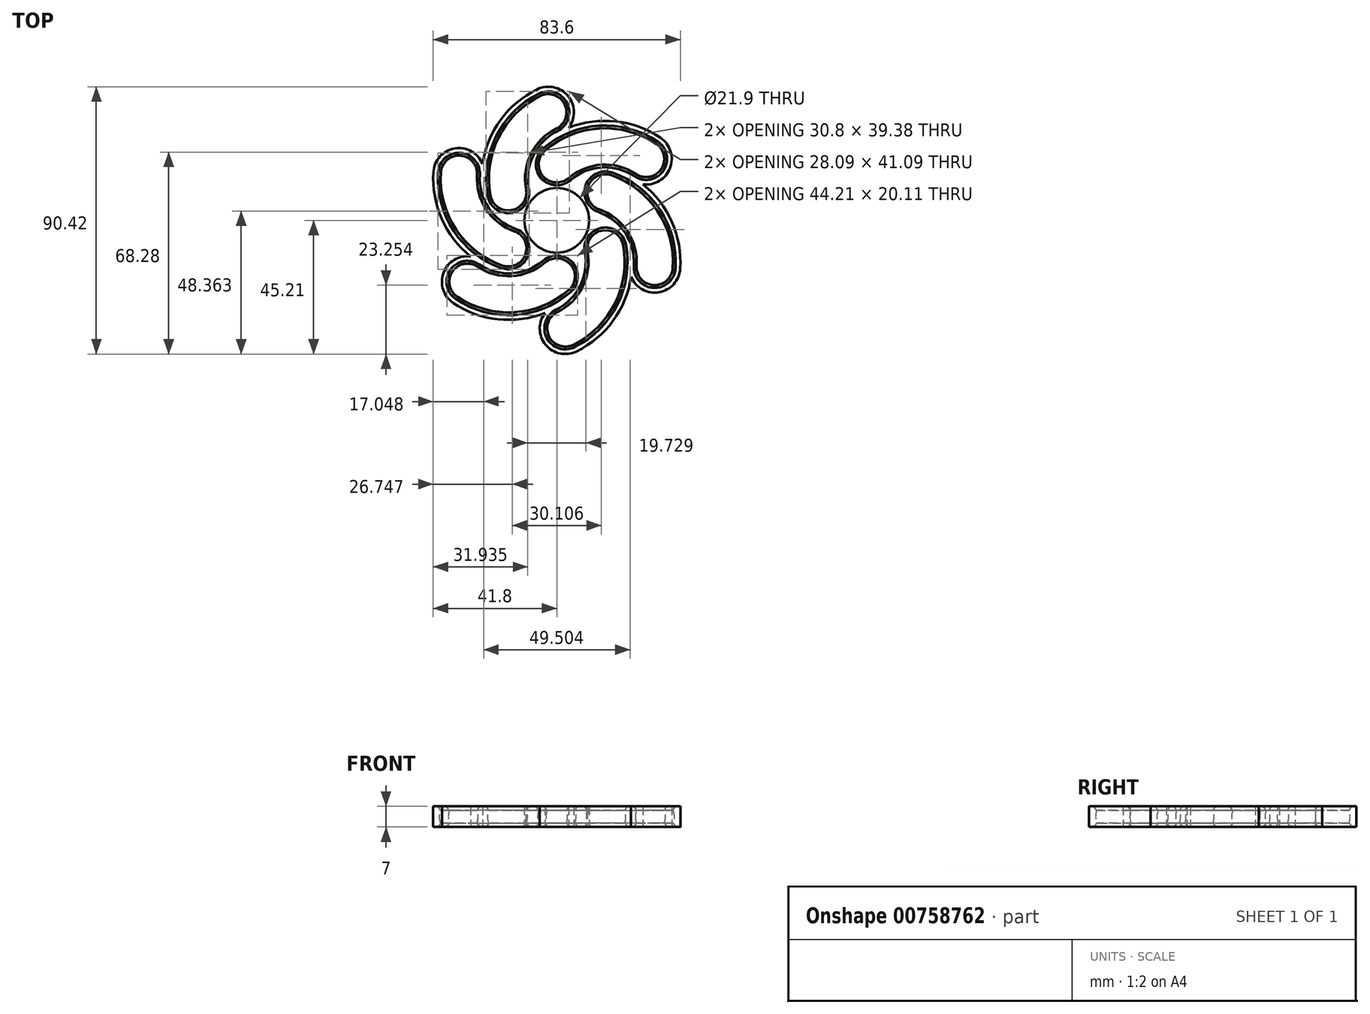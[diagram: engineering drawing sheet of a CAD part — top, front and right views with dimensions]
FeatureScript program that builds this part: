
annotation { "Feature Type Name" : "Feature", "Feature Type Description" : "" }
export const myFeature = defineFeature(function(context is Context, id is Id, definition is map)
    precondition{}
    {
        {
            var Q0;
            Q0=qCreatedBy(makeId("Top.planeOp"),FACE);
            var sketch = newSketch(context, id + "F0", { "sketchPlane" : qUnion([Q0])});
            skArc(sketch, "E0", {"start": v(6.97, 8.45) * mm, "mid": v(-0.32, 10.95) * mm, "end": v(-7.45, 8.02) * mm});
            skPoint(sketch, "E1", {"position": v(0, -24.5) * mm});
            skLineSegment(sketch, "E2", {"start": v(0, 0) * mm, "end": v(0, 18.95) * mm, "construction": true});
            skArc(sketch, "E3", {"start": v(25.4, 13.58) * mm, "mid": v(12.95, 16) * mm, "end": v(2.52, 8.78) * mm});
            skArc(sketch, "E4.0", {"start": v(30.22, 20.77) * mm, "mid": v(14.8, 24.95) * mm, "end": v(0, 18.95) * mm});
            skArc(sketch, "E5.0", {"start": v(35.03, 27.96) * mm, "mid": v(14.7, 33.61) * mm, "end": v(-5, 26.04) * mm});
            skArc(sketch, "E6", {"start": v(25.4, 13.58) * mm, "mid": v(37.4, 15.96) * mm, "end": v(35.03, 27.96) * mm});
            skArc(sketch, "E7.0", {"start": v(12.06, 14.62) * mm, "mid": v(0, 18.95) * mm, "end": v(-12.06, 14.62) * mm, "construction": true});
            skLineSegment(sketch, "E8", {"start": v(-7.45, 8.02) * mm, "end": v(-9.2, 16.57) * mm});
            skLineSegment(sketch, "E9", {"start": v(-9.2, 16.57) * mm, "end": v(-5, 26.04) * mm});
            skSolve(sketch);
        }
        {
            var Q0;
            {var subQ4=sQuery(id+"F0.wireOp",EDGE,"PiiM7Q08-lsxY-islm-UEzh-ksM0SnnuY6FK");Q0=makeQuery(id+"F0.imprint","IMPRINT",FACE,{"disambiguationData":[TD([[makeQuery(id+"F0.imprint","IMPRINT",EDGE,{"derivedFrom":subQ4}),-1.0]])]});}
            var Q1;
            Q1=makeQuery(id+"F0.imprint","IMPRINT",FACE,{"disambiguationData":[TD([[makeQuery(id+"F0.imprint","IMPRINT",EDGE,{"derivedFrom":sQuery(id+"F0.wireOp",EDGE,"E0")}),-1.0]])]});
            var Q2;
            {var subQ4=sQuery(id+"F0.wireOp",EDGE,"QqK0a54Q-URX9-TbrE-nkqz-KXdzGL0UVco7");Q2=makeQuery(id+"F0.imprint","IMPRINT",FACE,{"disambiguationData":[TD([[makeQuery(id+"F0.imprint","IMPRINT",EDGE,{"derivedFrom":subQ4}),-1.0]])]});}
            var Q3;
            {var subQ5=sQuery(id+"F0.wireOp",EDGE,"PiiM7Q08-lsxY-islm-UEzh-ksM0SnnuY6FK");Q3=makeQuery(id+"F0.imprint","IMPRINT",FACE,{"disambiguationData":[TD([[makeQuery(id+"F0.imprint","IMPRINT",EDGE,{"derivedFrom":subQ5}),1.0]])]});}
            var Q4;
            {var subQ1=sQuery(id+"F0.wireOp",EDGE,"E5.0");Q4=makeQuery(id+"F0.imprint","IMPRINT",FACE,{"disambiguationData":[TD([[makeQuery(id+"F0.imprint","IMPRINT",EDGE,{"derivedFrom":subQ1}),1.0]])]});}
            extrude(context, id + "F1", {"entities" : qUnion([Q0, Q1, Q2, Q3, Q4]), "endBound" : BoundingType.SYMMETRIC, "depth" : 7 * mm, "offsetDistance" : 25 * mm});
        }
        {
            var Q0;
            Q0=makeQuery(id+"F1.opExtrude","SWEPT_EDGE",EDGE,{"disambiguationData":[OSD([sQuery(id+"F0.wireOp",EDGE,"E3"),sQuery(id+"F0.wireOp",EDGE,"E6")])]});
            var Q1;
            Q1=sQuery(id+"F0.wireOp",VERTEX,"E5.0.start");
            cPlane(context, id + "F2", {"entities" : qUnion([Q0, Q1]), "cplaneType" : CPlaneType.LINE_ANGLE, "offset" : 25 * mm, "angle" : 0 * degree, "width" : 150 * mm, "height" : 150 * mm});
        }
        {
            var Q0;
            Q0=qCreatedBy(id+"F2.planeOp",FACE);
            var sketch = newSketch(context, id + "F3", { "sketchPlane" : qUnion([Q0])});
            skLineSegment(sketch, "E10", {"start": v(34.08, 6.5) * mm, "end": v(34.08, -6.5) * mm});
            skArc(sketch, "E11", {"start": v(34.08, -6.5) * mm, "mid": v(40.58, 0) * mm, "end": v(34.08, 6.5) * mm});
            skArc(sketch, "E12.MirrorCS", {"start": v(34.08, -6.5) * mm, "mid": v(27.58, 0) * mm, "end": v(34.08, 6.5) * mm});
            skSolve(sketch);
        }
        {
            var Q0;
            Q0=makeQuery(id+"F3.imprint","IMPRINT",FACE,{"disambiguationData":[TD([[makeQuery(id+"F3.imprint","IMPRINT",EDGE,{"derivedFrom":sQuery(id+"F3.wireOp",EDGE,"E10")}),1.0]])]});
            var Q1;
            Q1=makeQuery(id+"F3.imprint","IMPRINT",FACE,{"disambiguationData":[TD([[makeQuery(id+"F3.imprint","IMPRINT",EDGE,{"derivedFrom":sQuery(id+"F3.wireOp",EDGE,"E10")}),-1.0]])]});
            var Q2;
            Q2=sQuery(id+"F0.wireOp",EDGE,"E4.0");
            sweep(context, id + "F4", {"operationType" : NewBodyOperationType.REMOVE, "profiles" : qUnion([Q0, Q1]), "path" : qUnion([Q2])});
        }
        {
            var Q0;
            Q0=makeQuery(id+"F3.imprint","IMPRINT",FACE,{"disambiguationData":[TD([[makeQuery(id+"F3.imprint","IMPRINT",EDGE,{"derivedFrom":sQuery(id+"F3.wireOp",EDGE,"E10")}),1.0]])]});
            var Q1;
            Q1=sQuery(id+"F3.wireOp",EDGE,"E10");
            revolve(context, id + "F5", {"operationType" : NewBodyOperationType.REMOVE, "surfaceOperationType" : NewSurfaceOperationType.NEW, "entities" : qUnion([Q0]), "axis" : qUnion([Q1]), "revolveType" : RevolveType.ONE_DIRECTION, "angle" : 180 * degree});
        }
        {
            var Q0;
            Q0=makeQuery(id+"F4.boolean.opBoolean","COPY",FACE,{"derivedFrom":makeQuery(id+"F4.opSweep","CAP_FACE",FACE,{"disambiguationData":[OSD([sQuery(id+"F0.wireOp",VERTEX,"E4.0.end"),sQuery(id+"F3.wireOp",EDGE,"E11"),sQuery(id+"F3.wireOp",EDGE,"E12.MirrorCS")])],"isStart":false})});
            var sketch = newSketch(context, id + "F6", { "sketchPlane" : qUnion([Q0])});
            skLineSegment(sketch, "E13", {"start": v(20.86, 0) * mm, "end": v(7.86, 0) * mm});
            skArc(sketch, "E14", {"start": v(7.86, 0) * mm, "mid": v(14.36, -6.5) * mm, "end": v(20.86, 0) * mm});
            skSolve(sketch);
        }
        {
            var Q0;
            {var subQ1=makeQuery(id+"F4.boolean.opBoolean","INTERSECT",EDGE,{"derivedFrom":[makeQuery(id+"F1.opExtrude","CAP_FACE",FACE,{"disambiguationData":[OSD([sQuery(id+"F0.wireOp",EDGE,"E0"),sQuery(id+"F0.wireOp",EDGE,"Lb8NWhK4-ym9p-KzVv-z8Fr-7k6zUVGv0M9w"),sQuery(id+"F0.wireOp",EDGE,"QqK0a54Q-URX9-TbrE-nkqz-KXdzGL0UVco7"),sQuery(id+"F0.wireOp",EDGE,"E3"),sQuery(id+"F0.wireOp",EDGE,"E5.0"),sQuery(id+"F0.wireOp",EDGE,"E6"),sQuery(id+"F0.wireOp",EDGE,"nqTzWoM8-xc7r-Lhgo-26Yi-vVSrXjbg86Ji")])],"isStart":true}),makeQuery(id+"F4.opSweep","CAP_FACE",FACE,{"disambiguationData":[OSD([sQuery(id+"F0.wireOp",VERTEX,"I2wmlmdm-DSrS-oub0-GOcV-EtuJTHkaWZzk.end"),sQuery(id+"F3.wireOp",EDGE,"E11"),sQuery(id+"F3.wireOp",EDGE,"E12.MirrorCS")])],"isStart":false})]});Q0=makeQuery(id+"F6.imprint","IMPRINT",FACE,{"disambiguationData":[TD([[makeQuery(id+"F6.imprint","IMPRINT",EDGE,{"derivedFrom":subQ1}),-1.0]])]});}
            var Q1;
            {var subQ0=sQuery(id+"F6.wireOp",EDGE,"E13");Q1=makeQuery(id+"F6.imprint","IMPRINT",FACE,{"disambiguationData":[TD([[makeQuery(id+"F6.imprint","IMPRINT",EDGE,{"derivedFrom":subQ0}),1.0]])]});}
            var Q2;
            Q2=sQuery(id+"F6.wireOp",EDGE,"E13");
            revolve(context, id + "F7", {"operationType" : NewBodyOperationType.REMOVE, "surfaceOperationType" : NewSurfaceOperationType.NEW, "entities" : qUnion([Q0, Q1]), "axis" : qUnion([Q2]), "revolveType" : RevolveType.FULL, "oppositeDirection" : true});
        }
        {
            var Q0;
            Q0=qCreatedBy(makeId("Front.planeOp"),FACE);
            var sketch = newSketch(context, id + "F8", { "sketchPlane" : qUnion([Q0])});
            skLineSegment(sketch, "E15", {"start": v(0, -9.37) * mm, "end": v(0, 10.86) * mm, "construction": true});
            skSolve(sketch);
        }
        {
            var Q0;
            Q0=makeQuery(id+"F1.opExtrude","SWEPT_BODY",BODY,{"disambiguationData":[OSD([sQuery(id+"F0.wireOp",EDGE,"E0"),sQuery(id+"F0.wireOp",EDGE,"Lb8NWhK4-ym9p-KzVv-z8Fr-7k6zUVGv0M9w"),sQuery(id+"F0.wireOp",EDGE,"QqK0a54Q-URX9-TbrE-nkqz-KXdzGL0UVco7"),sQuery(id+"F0.wireOp",EDGE,"E3"),sQuery(id+"F0.wireOp",EDGE,"E5.0"),sQuery(id+"F0.wireOp",EDGE,"E6"),sQuery(id+"F0.wireOp",EDGE,"nqTzWoM8-xc7r-Lhgo-26Yi-vVSrXjbg86Ji")])]});
            var Q1;
            Q1=sQuery(id+"F8.wireOp",EDGE,"E15");
            circularPattern(context, id + "F9", {"operationType" : NewBodyOperationType.ADD, "entities" : qUnion([Q0]), "axis" : qUnion([Q1]), "angle" : 360 * degree, "instanceCount" : 6, "equalSpace" : true});
        }
        {
            var Q0;
            Q0=makeQuery(id+"F9.opPattern","COPY",EDGE,{"derivedFrom":makeQuery(id+"F4.boolean.opBoolean","INTERSECT",EDGE,{"disambiguationData":[OD(1.0)],"derivedFrom":[makeQuery(id+"F1.opExtrude","CAP_FACE",FACE,{"disambiguationData":[OSD([sQuery(id+"F0.wireOp",EDGE,"E0"),sQuery(id+"F0.wireOp",EDGE,"E3"),sQuery(id+"F0.wireOp",EDGE,"E5.0"),sQuery(id+"F0.wireOp",EDGE,"E6"),sQuery(id+"F0.wireOp",EDGE,"nqTzWoM8-xc7r-Lhgo-26Yi-vVSrXjbg86Ji")])],"isStart":false}),makeQuery(id+"F4.opSweep","SWEPT_FACE",FACE,{"disambiguationData":[OSD([sQuery(id+"F0.wireOp",EDGE,"E4.0"),sQuery(id+"F3.wireOp",EDGE,"E11"),sQuery(id+"F3.wireOp",EDGE,"E12.MirrorCS")])]})]}),"instanceName":"3"});
            var Q1;
            Q1=makeQuery(id+"F9.opPattern","COPY",EDGE,{"derivedFrom":makeQuery(id+"F4.boolean.opBoolean","INTERSECT",EDGE,{"disambiguationData":[OD(0.0)],"derivedFrom":[makeQuery(id+"F1.opExtrude","CAP_FACE",FACE,{"disambiguationData":[OSD([sQuery(id+"F0.wireOp",EDGE,"E0"),sQuery(id+"F0.wireOp",EDGE,"E3"),sQuery(id+"F0.wireOp",EDGE,"E5.0"),sQuery(id+"F0.wireOp",EDGE,"E6"),sQuery(id+"F0.wireOp",EDGE,"nqTzWoM8-xc7r-Lhgo-26Yi-vVSrXjbg86Ji")])],"isStart":false}),makeQuery(id+"F4.opSweep","SWEPT_FACE",FACE,{"disambiguationData":[OSD([sQuery(id+"F0.wireOp",EDGE,"E4.0"),sQuery(id+"F3.wireOp",EDGE,"E11"),sQuery(id+"F3.wireOp",EDGE,"E12.MirrorCS")])]})]}),"instanceName":"4"});
            var Q2;
            Q2=makeQuery(id+"F9.opPattern","COPY",EDGE,{"derivedFrom":makeQuery(id+"F4.boolean.opBoolean","INTERSECT",EDGE,{"disambiguationData":[OD(1.0)],"derivedFrom":[makeQuery(id+"F1.opExtrude","CAP_FACE",FACE,{"disambiguationData":[OSD([sQuery(id+"F0.wireOp",EDGE,"E0"),sQuery(id+"F0.wireOp",EDGE,"E3"),sQuery(id+"F0.wireOp",EDGE,"E5.0"),sQuery(id+"F0.wireOp",EDGE,"E6"),sQuery(id+"F0.wireOp",EDGE,"nqTzWoM8-xc7r-Lhgo-26Yi-vVSrXjbg86Ji")])],"isStart":false}),makeQuery(id+"F4.opSweep","SWEPT_FACE",FACE,{"disambiguationData":[OSD([sQuery(id+"F0.wireOp",EDGE,"E4.0"),sQuery(id+"F3.wireOp",EDGE,"E11"),sQuery(id+"F3.wireOp",EDGE,"E12.MirrorCS")])]})]}),"instanceName":"5"});
            var Q3;
            Q3=makeQuery(id+"F9.opPattern","COPY",EDGE,{"derivedFrom":makeQuery(id+"F4.boolean.opBoolean","INTERSECT",EDGE,{"disambiguationData":[OD(0.0)],"derivedFrom":[makeQuery(id+"F1.opExtrude","CAP_FACE",FACE,{"disambiguationData":[OSD([sQuery(id+"F0.wireOp",EDGE,"E0"),sQuery(id+"F0.wireOp",EDGE,"E3"),sQuery(id+"F0.wireOp",EDGE,"E5.0"),sQuery(id+"F0.wireOp",EDGE,"E6"),sQuery(id+"F0.wireOp",EDGE,"nqTzWoM8-xc7r-Lhgo-26Yi-vVSrXjbg86Ji")])],"isStart":false}),makeQuery(id+"F4.opSweep","SWEPT_FACE",FACE,{"disambiguationData":[OSD([sQuery(id+"F0.wireOp",EDGE,"E4.0"),sQuery(id+"F3.wireOp",EDGE,"E11"),sQuery(id+"F3.wireOp",EDGE,"E12.MirrorCS")])]})]}),"instanceName":"6"});
            var Q4;
            Q4=makeQuery(id+"F4.boolean.opBoolean","INTERSECT",EDGE,{"disambiguationData":[OD(0.0)],"derivedFrom":[makeQuery(id+"F1.opExtrude","CAP_FACE",FACE,{"disambiguationData":[OSD([sQuery(id+"F0.wireOp",EDGE,"E0"),sQuery(id+"F0.wireOp",EDGE,"E3"),sQuery(id+"F0.wireOp",EDGE,"E5.0"),sQuery(id+"F0.wireOp",EDGE,"E6"),sQuery(id+"F0.wireOp",EDGE,"nqTzWoM8-xc7r-Lhgo-26Yi-vVSrXjbg86Ji")])],"isStart":false}),makeQuery(id+"F4.opSweep","SWEPT_FACE",FACE,{"disambiguationData":[OSD([sQuery(id+"F0.wireOp",EDGE,"E4.0"),sQuery(id+"F3.wireOp",EDGE,"E11"),sQuery(id+"F3.wireOp",EDGE,"E12.MirrorCS")])]})]});
            var Q5;
            Q5=makeQuery(id+"F9.opPattern","COPY",EDGE,{"derivedFrom":makeQuery(id+"F4.boolean.opBoolean","INTERSECT",EDGE,{"disambiguationData":[OD(0.0)],"derivedFrom":[makeQuery(id+"F1.opExtrude","CAP_FACE",FACE,{"disambiguationData":[OSD([sQuery(id+"F0.wireOp",EDGE,"E0"),sQuery(id+"F0.wireOp",EDGE,"E3"),sQuery(id+"F0.wireOp",EDGE,"E5.0"),sQuery(id+"F0.wireOp",EDGE,"E6"),sQuery(id+"F0.wireOp",EDGE,"nqTzWoM8-xc7r-Lhgo-26Yi-vVSrXjbg86Ji")])],"isStart":false}),makeQuery(id+"F4.opSweep","SWEPT_FACE",FACE,{"disambiguationData":[OSD([sQuery(id+"F0.wireOp",EDGE,"E4.0"),sQuery(id+"F3.wireOp",EDGE,"E11"),sQuery(id+"F3.wireOp",EDGE,"E12.MirrorCS")])]})]}),"instanceName":"1"});
            var Q6;
            Q6=makeQuery(id+"F9.opPattern","COPY",EDGE,{"derivedFrom":makeQuery(id+"F4.boolean.opBoolean","INTERSECT",EDGE,{"disambiguationData":[OD(0.0)],"derivedFrom":[makeQuery(id+"F1.opExtrude","CAP_FACE",FACE,{"disambiguationData":[OSD([sQuery(id+"F0.wireOp",EDGE,"E0"),sQuery(id+"F0.wireOp",EDGE,"E3"),sQuery(id+"F0.wireOp",EDGE,"E5.0"),sQuery(id+"F0.wireOp",EDGE,"E6"),sQuery(id+"F0.wireOp",EDGE,"nqTzWoM8-xc7r-Lhgo-26Yi-vVSrXjbg86Ji")])],"isStart":false}),makeQuery(id+"F4.opSweep","SWEPT_FACE",FACE,{"disambiguationData":[OSD([sQuery(id+"F0.wireOp",EDGE,"E4.0"),sQuery(id+"F3.wireOp",EDGE,"E11"),sQuery(id+"F3.wireOp",EDGE,"E12.MirrorCS")])]})]}),"instanceName":"2"});
            var Q7;
            Q7=makeQuery(id+"F9.opPattern","COPY",EDGE,{"derivedFrom":makeQuery(id+"F4.boolean.opBoolean","INTERSECT",EDGE,{"disambiguationData":[OD(1.0)],"derivedFrom":[makeQuery(id+"F1.opExtrude","CAP_FACE",FACE,{"disambiguationData":[OSD([sQuery(id+"F0.wireOp",EDGE,"E0"),sQuery(id+"F0.wireOp",EDGE,"E3"),sQuery(id+"F0.wireOp",EDGE,"E5.0"),sQuery(id+"F0.wireOp",EDGE,"E6"),sQuery(id+"F0.wireOp",EDGE,"nqTzWoM8-xc7r-Lhgo-26Yi-vVSrXjbg86Ji")])],"isStart":true}),makeQuery(id+"F4.opSweep","SWEPT_FACE",FACE,{"disambiguationData":[OSD([sQuery(id+"F0.wireOp",EDGE,"E4.0"),sQuery(id+"F3.wireOp",EDGE,"E11"),sQuery(id+"F3.wireOp",EDGE,"E12.MirrorCS")])]})]}),"instanceName":"4"});
            var Q8;
            Q8=makeQuery(id+"F9.opPattern","COPY",EDGE,{"derivedFrom":makeQuery(id+"F4.boolean.opBoolean","INTERSECT",EDGE,{"disambiguationData":[OD(0.0)],"derivedFrom":[makeQuery(id+"F1.opExtrude","CAP_FACE",FACE,{"disambiguationData":[OSD([sQuery(id+"F0.wireOp",EDGE,"E0"),sQuery(id+"F0.wireOp",EDGE,"E3"),sQuery(id+"F0.wireOp",EDGE,"E5.0"),sQuery(id+"F0.wireOp",EDGE,"E6"),sQuery(id+"F0.wireOp",EDGE,"nqTzWoM8-xc7r-Lhgo-26Yi-vVSrXjbg86Ji")])],"isStart":true}),makeQuery(id+"F4.opSweep","SWEPT_FACE",FACE,{"disambiguationData":[OSD([sQuery(id+"F0.wireOp",EDGE,"E4.0"),sQuery(id+"F3.wireOp",EDGE,"E11"),sQuery(id+"F3.wireOp",EDGE,"E12.MirrorCS")])]})]}),"instanceName":"5"});
            var Q9;
            Q9=makeQuery(id+"F9.opPattern","COPY",EDGE,{"derivedFrom":makeQuery(id+"F4.boolean.opBoolean","INTERSECT",EDGE,{"disambiguationData":[OD(0.0)],"derivedFrom":[makeQuery(id+"F1.opExtrude","CAP_FACE",FACE,{"disambiguationData":[OSD([sQuery(id+"F0.wireOp",EDGE,"E0"),sQuery(id+"F0.wireOp",EDGE,"E3"),sQuery(id+"F0.wireOp",EDGE,"E5.0"),sQuery(id+"F0.wireOp",EDGE,"E6"),sQuery(id+"F0.wireOp",EDGE,"nqTzWoM8-xc7r-Lhgo-26Yi-vVSrXjbg86Ji")])],"isStart":true}),makeQuery(id+"F4.opSweep","SWEPT_FACE",FACE,{"disambiguationData":[OSD([sQuery(id+"F0.wireOp",EDGE,"E4.0"),sQuery(id+"F3.wireOp",EDGE,"E11"),sQuery(id+"F3.wireOp",EDGE,"E12.MirrorCS")])]})]}),"instanceName":"6"});
            var Q10;
            Q10=makeQuery(id+"F4.boolean.opBoolean","INTERSECT",EDGE,{"disambiguationData":[OD(0.0)],"derivedFrom":[makeQuery(id+"F1.opExtrude","CAP_FACE",FACE,{"disambiguationData":[OSD([sQuery(id+"F0.wireOp",EDGE,"E0"),sQuery(id+"F0.wireOp",EDGE,"E3"),sQuery(id+"F0.wireOp",EDGE,"E5.0"),sQuery(id+"F0.wireOp",EDGE,"E6"),sQuery(id+"F0.wireOp",EDGE,"nqTzWoM8-xc7r-Lhgo-26Yi-vVSrXjbg86Ji")])],"isStart":true}),makeQuery(id+"F4.opSweep","SWEPT_FACE",FACE,{"disambiguationData":[OSD([sQuery(id+"F0.wireOp",EDGE,"E4.0"),sQuery(id+"F3.wireOp",EDGE,"E11"),sQuery(id+"F3.wireOp",EDGE,"E12.MirrorCS")])]})]});
            var Q11;
            Q11=makeQuery(id+"F9.opPattern","COPY",EDGE,{"derivedFrom":makeQuery(id+"F4.boolean.opBoolean","INTERSECT",EDGE,{"disambiguationData":[OD(0.0)],"derivedFrom":[makeQuery(id+"F1.opExtrude","CAP_FACE",FACE,{"disambiguationData":[OSD([sQuery(id+"F0.wireOp",EDGE,"E0"),sQuery(id+"F0.wireOp",EDGE,"E3"),sQuery(id+"F0.wireOp",EDGE,"E5.0"),sQuery(id+"F0.wireOp",EDGE,"E6"),sQuery(id+"F0.wireOp",EDGE,"nqTzWoM8-xc7r-Lhgo-26Yi-vVSrXjbg86Ji")])],"isStart":true}),makeQuery(id+"F4.opSweep","SWEPT_FACE",FACE,{"disambiguationData":[OSD([sQuery(id+"F0.wireOp",EDGE,"E4.0"),sQuery(id+"F3.wireOp",EDGE,"E11"),sQuery(id+"F3.wireOp",EDGE,"E12.MirrorCS")])]})]}),"instanceName":"1"});
            var Q12;
            Q12=makeQuery(id+"F9.opPattern","COPY",EDGE,{"derivedFrom":makeQuery(id+"F4.boolean.opBoolean","INTERSECT",EDGE,{"disambiguationData":[OD(0.0)],"derivedFrom":[makeQuery(id+"F1.opExtrude","CAP_FACE",FACE,{"disambiguationData":[OSD([sQuery(id+"F0.wireOp",EDGE,"E0"),sQuery(id+"F0.wireOp",EDGE,"E3"),sQuery(id+"F0.wireOp",EDGE,"E5.0"),sQuery(id+"F0.wireOp",EDGE,"E6"),sQuery(id+"F0.wireOp",EDGE,"nqTzWoM8-xc7r-Lhgo-26Yi-vVSrXjbg86Ji")])],"isStart":true}),makeQuery(id+"F4.opSweep","SWEPT_FACE",FACE,{"disambiguationData":[OSD([sQuery(id+"F0.wireOp",EDGE,"E4.0"),sQuery(id+"F3.wireOp",EDGE,"E11"),sQuery(id+"F3.wireOp",EDGE,"E12.MirrorCS")])]})]}),"instanceName":"2"});
            var Q13;
            Q13=makeQuery(id+"F9.opPattern","COPY",EDGE,{"derivedFrom":makeQuery(id+"F4.boolean.opBoolean","INTERSECT",EDGE,{"disambiguationData":[OD(0.0)],"derivedFrom":[makeQuery(id+"F1.opExtrude","CAP_FACE",FACE,{"disambiguationData":[OSD([sQuery(id+"F0.wireOp",EDGE,"E0"),sQuery(id+"F0.wireOp",EDGE,"E3"),sQuery(id+"F0.wireOp",EDGE,"E5.0"),sQuery(id+"F0.wireOp",EDGE,"E6"),sQuery(id+"F0.wireOp",EDGE,"nqTzWoM8-xc7r-Lhgo-26Yi-vVSrXjbg86Ji")])],"isStart":true}),makeQuery(id+"F4.opSweep","SWEPT_FACE",FACE,{"disambiguationData":[OSD([sQuery(id+"F0.wireOp",EDGE,"E4.0"),sQuery(id+"F3.wireOp",EDGE,"E11"),sQuery(id+"F3.wireOp",EDGE,"E12.MirrorCS")])]})]}),"instanceName":"3"});
            chamfer(context, id + "F10", {"entities" : qUnion([Q0, Q1, Q2, Q3, Q4, Q5, Q6, Q7, Q8, Q9, Q10, Q11, Q12, Q13]), "width" : 1 * mm, "tangentPropagation" : true});
        }
    });
